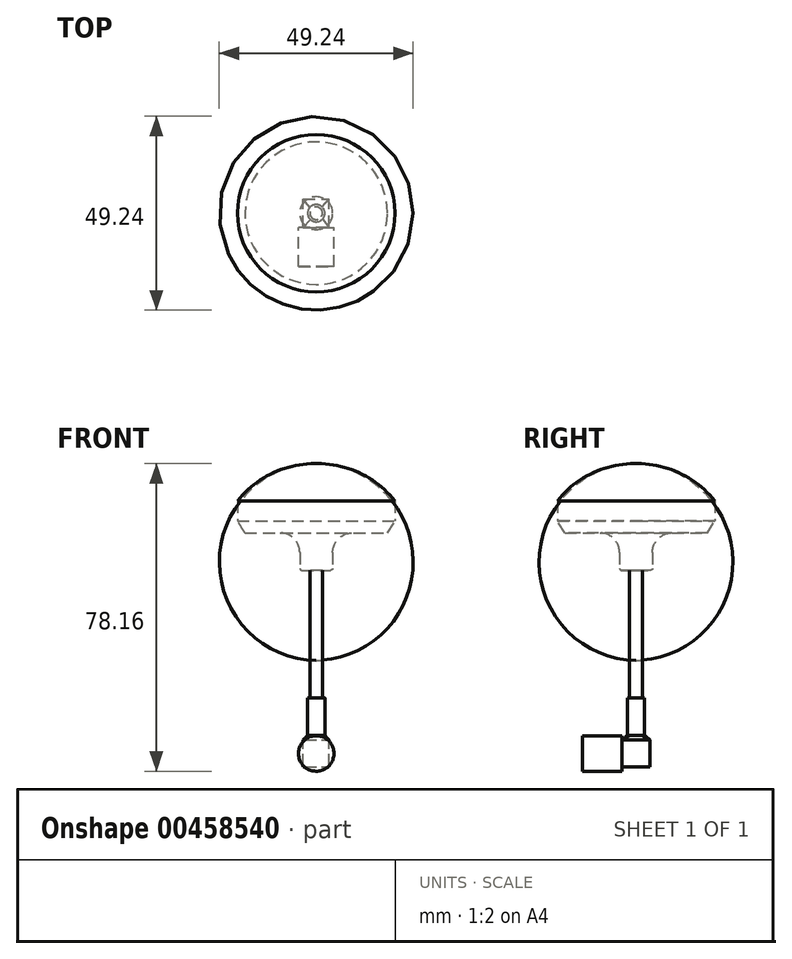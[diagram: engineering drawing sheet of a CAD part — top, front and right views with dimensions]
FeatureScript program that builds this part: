
annotation { "Feature Type Name" : "Feature", "Feature Type Description" : "" }
export const myFeature = defineFeature(function(context is Context, id is Id, definition is map)
    precondition{}
    {
        {
            var Q0;
            Q0=qCreatedBy(makeId("Right.planeOp"),FACE);
            var sketch = newSketch(context, id + "F0", { "sketchPlane" : qUnion([Q0])});
            skLineSegment(sketch, "E0", {"start": v(18.1, 0) * mm, "end": v(9.17, 0) * mm});
            skLineSegment(sketch, "E1", {"start": v(4.17, -5) * mm, "end": v(4.17, -9) * mm});
            skLineSegment(sketch, "E2", {"start": v(3.68, -9.5) * mm, "end": v(0, -9.5) * mm});
            skLineSegment(sketch, "E3", {"start": v(0, -9.5) * mm, "end": v(0, 17.6) * mm});
            skPoint(sketch, "E4.visualSharp", {"position": v(4.17, 0) * mm});
            skArc(sketch, "E4.filletArc", {"start": v(9.17, 0) * mm, "mid": v(5.64, -1.46) * mm, "end": v(4.17, -5) * mm});
            skLineSegment(sketch, "E5", {"start": v(18.1, 0) * mm, "end": v(20, 3) * mm});
            skLineSegment(sketch, "E6", {"start": v(20, 3) * mm, "end": v(20, 8.1) * mm});
            skArc(sketch, "E7", {"start": v(20, 8.1) * mm, "mid": v(11.1, 15.18) * mm, "end": v(0, 17.6) * mm});
            skPoint(sketch, "E8.visualSharp", {"position": v(4.17, -9.5) * mm});
            skArc(sketch, "E8.filletArc", {"start": v(3.68, -9.5) * mm, "mid": v(4.03, -9.35) * mm, "end": v(4.17, -9) * mm});
            skSolve(sketch);
        }
        {
            var Q0;
            Q0=qSketchRegion(id+"F0",true);
            var Q1;
            Q1=sQuery(id+"F0.wireOp",EDGE,"E3");
            revolve(context, id + "F1", {"entities" : qUnion([Q0]), "axis" : qUnion([Q1]), "revolveType" : RevolveType.FULL});
        }
        {
            var Q0;
            Q0=makeQuery(id+"F1.opRevolve","SWEPT_FACE",FACE,{"disambiguationData":[OSD([sQuery(id+"F0.wireOp",EDGE,"E2")])]});
            var sketch = newSketch(context, id + "F2", { "sketchPlane" : qUnion([Q0])});
            skCircle(sketch, "E9", {"center": v(0, 0) * mm, "radius": 1.6 * mm});
            skSolve(sketch);
        }
        {
            var Q0;
            Q0=qSketchRegion(id+"F2",true);
            extrude(context, id + "F3", {"entities" : qUnion([Q0]), "operationType" : NewBodyOperationType.ADD, "depth" : 32.4 * mm});
        }
        {
            var Q0;
            Q0=makeQuery(id+"F3.opExtrude","CAP_FACE",FACE,{"disambiguationData":[OSD([sQuery(id+"F2.wireOp",EDGE,"E9")])],"isStart":false});
            var sketch = newSketch(context, id + "F4", { "sketchPlane" : qUnion([Q0])});
            skCircle(sketch, "E10", {"center": v(0, 0) * mm, "radius": 2.2 * mm});
            skSolve(sketch);
        }
        {
            var Q0;
            Q0=qSketchRegion(id+"F4",true);
            extrude(context, id + "F5", {"entities" : qUnion([Q0]), "operationType" : NewBodyOperationType.ADD, "depth" : 9.5 * mm});
        }
        {
            var Q0;
            Q0=makeQuery(id+"F5.opExtrude","CAP_FACE",FACE,{"disambiguationData":[OSD([sQuery(id+"F4.wireOp",EDGE,"E10")])],"isStart":false});
            cPlane(context, id + "F6", {"entities" : qUnion([Q0]), "cplaneType" : CPlaneType.OFFSET, "offset" : 1.25 * mm, "width" : 150 * mm, "height" : 150 * mm});
        }
        {
            var Q0;
            Q0=qCreatedBy(id+"F6.planeOp",FACE);
            var sketch = newSketch(context, id + "F7", { "sketchPlane" : qUnion([Q0])});
            skLineSegment(sketch, "E11.bottom", {"start": v(-3.3, 3.6) * mm, "end": v(3.3, 3.6) * mm});
            skLineSegment(sketch, "E11.top", {"start": v(-3.3, -3.6) * mm, "end": v(3.3, -3.6) * mm});
            skLineSegment(sketch, "E11.left", {"start": v(-3.3, 3.6) * mm, "end": v(-3.3, -3.6) * mm});
            skLineSegment(sketch, "E11.right", {"start": v(3.3, 3.6) * mm, "end": v(3.3, -3.6) * mm});
            skPoint(sketch, "E11.middle", {"position": v(0, 0) * mm});
            skSolve(sketch);
        }
        {
            var Q0;
            Q0=qSketchRegion(id+"F7",true);
            extrude(context, id + "F8", {"entities" : qUnion([Q0]), "operationType" : NewBodyOperationType.ADD, "depth" : 6.8 * mm});
        }
        {
            var Q2;
            Q2=makeQuery(id+"F5.opExtrude","CAP_FACE",FACE,{"disambiguationData":[OSD([sQuery(id+"F4.wireOp",EDGE,"E10")])],"isStart":false});
            var Q3;
            Q3=makeQuery(id+"F8.opExtrude","CAP_FACE",FACE,{"disambiguationData":[OSD([sQuery(id+"F7.wireOp",EDGE,"E11.bottom"),sQuery(id+"F7.wireOp",EDGE,"E11.top"),sQuery(id+"F7.wireOp",EDGE,"E11.left"),sQuery(id+"F7.wireOp",EDGE,"E11.right")])],"isStart":true});
            loft(context, id + "F9", {"operationType" : NewBodyOperationType.ADD, "sheetProfilesArray" : [{ "sheetProfileEntities" : qUnion([Q2]) }, { "sheetProfileEntities" : qUnion([Q3]) }]});
        }
        {
            var Q0;
            Q0=makeQuery(id+"F8.opExtrude","SWEPT_FACE",FACE,{"disambiguationData":[OSD([sQuery(id+"F7.wireOp",EDGE,"E11.bottom")])]});
            var sketch = newSketch(context, id + "F10", { "sketchPlane" : qUnion([Q0])});
            skCircle(sketch, "E12", {"center": v(0, -56.05) * mm, "radius": 4.5 * mm});
            skLineSegment(sketch, "E13", {"start": v(0, -56.05) * mm, "end": v(0, -59.45) * mm, "construction": true});
            skLineSegment(sketch, "E14", {"start": v(0, -56.05) * mm, "end": v(0, -52.65) * mm, "construction": true});
            skSolve(sketch);
        }
        {
            var Q0;
            Q0=qSketchRegion(id+"F10",true);
            extrude(context, id + "F11", {"entities" : qUnion([Q0]), "operationType" : NewBodyOperationType.ADD, "depth" : 10 * mm});
        }
    });
